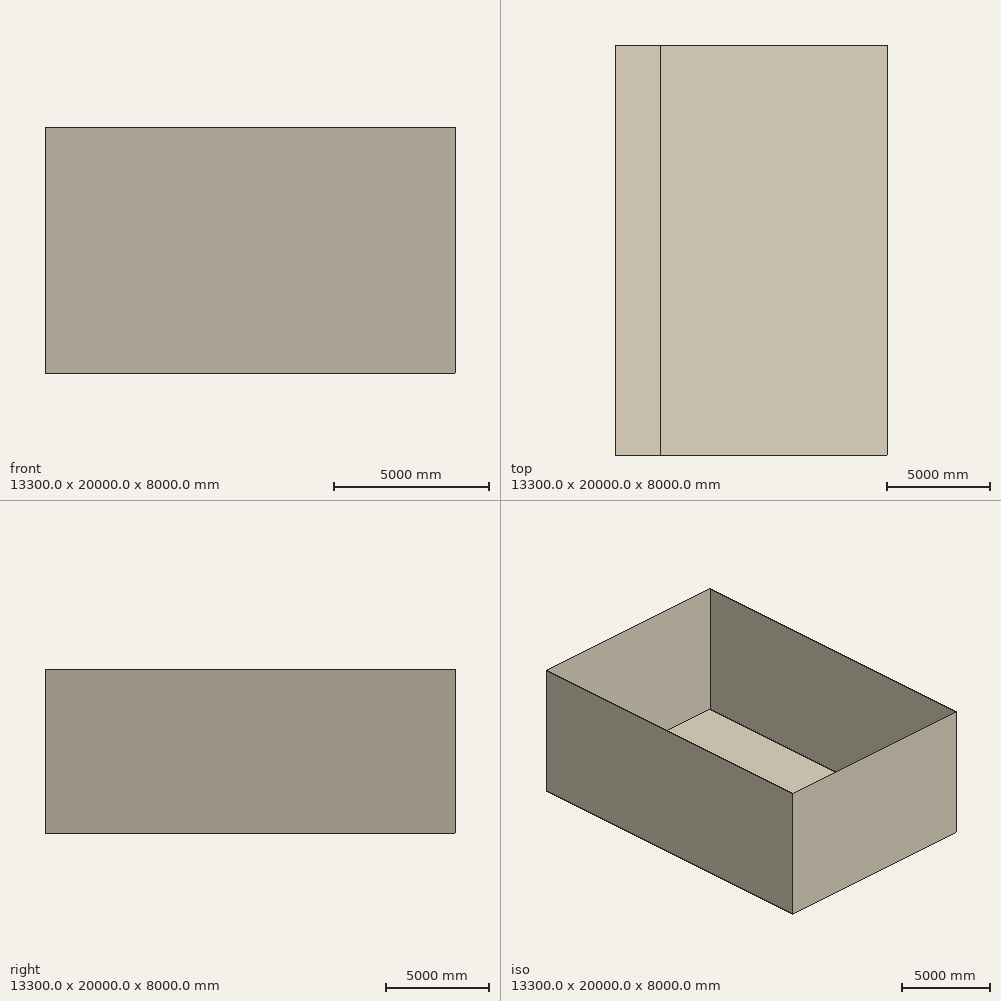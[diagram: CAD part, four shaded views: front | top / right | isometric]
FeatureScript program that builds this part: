
annotation { "Feature Type Name" : "Feature", "Feature Type Description" : "" }
export const myFeature = defineFeature(function(context is Context, id is Id, definition is map)
    precondition{}
    {
        {
            var Q0;
            Q0=qCreatedBy(makeId("Top.planeOp"),FACE);
            var sketch = newSketch(context, id + "F0", { "sketchPlane" : qUnion([Q0])});
            skLineSegment(sketch, "E0.bottom", {"start": v(-6650.32, 10447.53) * mm, "end": v(6649.68, 10447.53) * mm});
            skLineSegment(sketch, "E0.top", {"start": v(-6650.32, -9552.47) * mm, "end": v(6649.68, -9552.47) * mm});
            skLineSegment(sketch, "E0.left", {"start": v(-6650.32, 10447.53) * mm, "end": v(-6650.32, -9552.47) * mm});
            skLineSegment(sketch, "E0.right", {"start": v(6649.68, 10447.53) * mm, "end": v(6649.68, -9552.47) * mm});
            skSolve(sketch);
        }
        {
            var Q0;
            Q0=makeQuery(id+"F0.imprint","IMPRINT",FACE,{"disambiguationData":[TD([[makeQuery(id+"F0.imprint","IMPRINT",EDGE,{"derivedFrom":sQuery(id+"F0.wireOp",EDGE,"E0.bottom")}),-1.0]])]});
            extrude(context, id + "F1", {"entities" : qUnion([Q0]), "depth" : 8000 * mm});
        }
        {
            var Q0;
            Q0=makeQuery(id+"F1.opExtrude","CAP_FACE",FACE,{"disambiguationData":[OSD([sQuery(id+"F0.wireOp",EDGE,"E0.bottom"),sQuery(id+"F0.wireOp",EDGE,"E0.top"),sQuery(id+"F0.wireOp",EDGE,"E0.left"),sQuery(id+"F0.wireOp",EDGE,"E0.right")])],"isStart":false});
            shell(context, id + "F2", {"entities" : qUnion([Q0]), "thickness" : 2.5 * mm});
        }
        {
            var Q0;
            Q0=makeQuery(id+"F2.opShell","OFFSET_FACE",FACE,{"disambiguationData":[OSD([sQuery(id+"F0.wireOp",EDGE,"E0.left")])]});
            var sketch = newSketch(context, id + "F3", { "sketchPlane" : qUnion([Q0])});
            skLineSegment(sketch, "E1.bottom", {"start": v(10445.03, 5641.5) * mm, "end": v(-9549.97, 5641.5) * mm});
            skLineSegment(sketch, "E1.top", {"start": v(10445.03, 4001.25) * mm, "end": v(-9549.97, 4001.25) * mm});
            skLineSegment(sketch, "E1.left", {"start": v(10445.03, 5641.5) * mm, "end": v(10445.03, 4001.25) * mm});
            skLineSegment(sketch, "E1.right", {"start": v(-9549.97, 5641.5) * mm, "end": v(-9549.97, 4001.25) * mm});
            skSolve(sketch);
        }
        {
            var Q0;
            Q0=makeQuery(id+"F3.imprint","IMPRINT",FACE,{"disambiguationData":[TD([[makeQuery(id+"F3.imprint","IMPRINT",EDGE,{"derivedFrom":sQuery(id+"F3.wireOp",EDGE,"E1.bottom")}),1.0]])]});
            extrude(context, id + "F4", {"entities" : qUnion([Q0]), "operationType" : NewBodyOperationType.ADD, "depth" : 2200 * mm});
        }
    });
